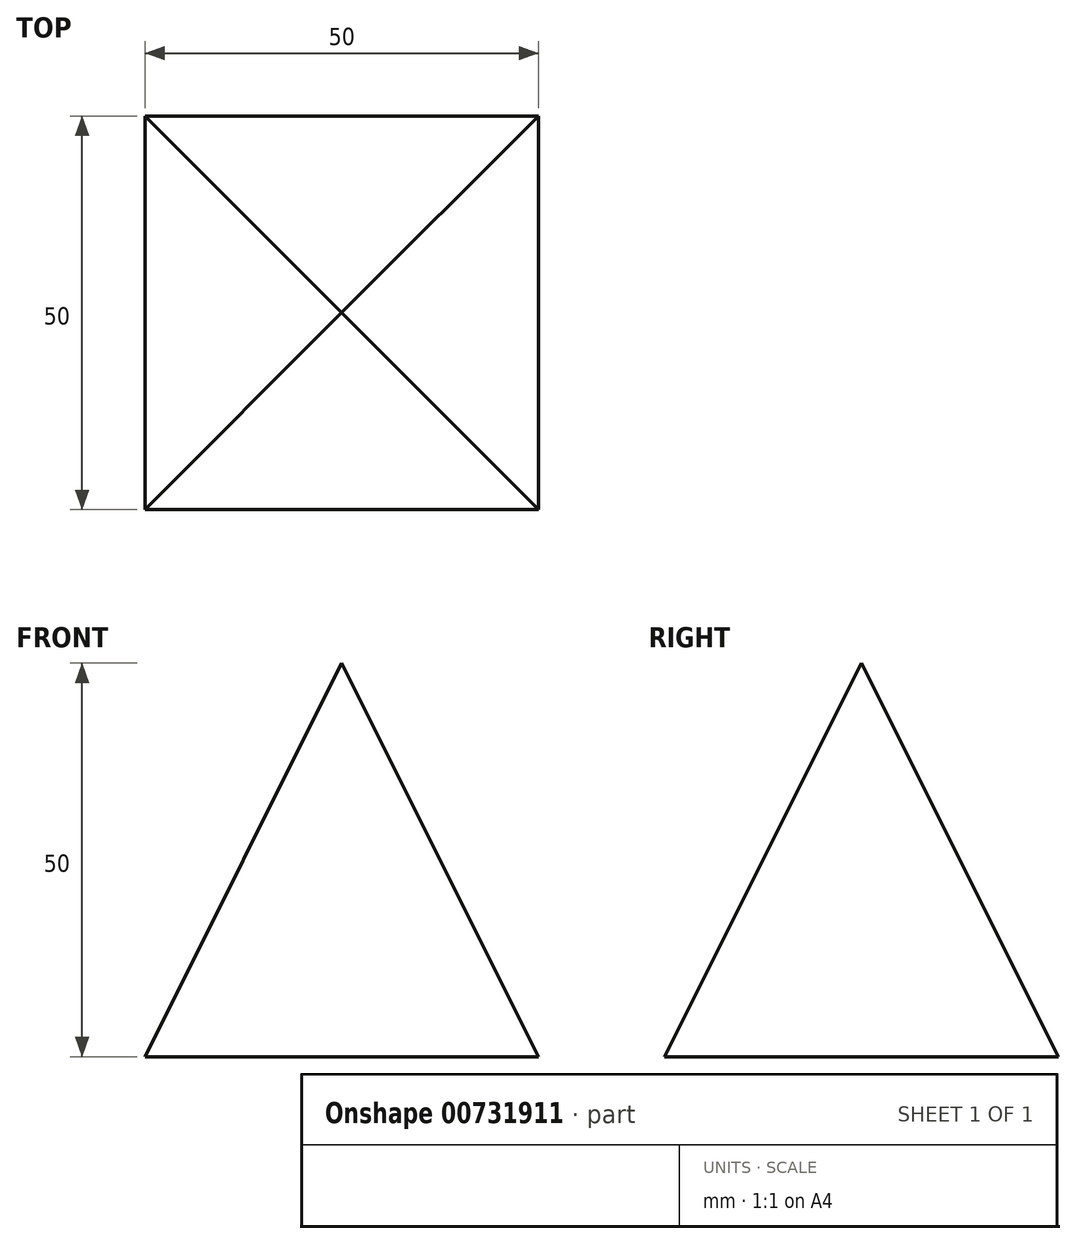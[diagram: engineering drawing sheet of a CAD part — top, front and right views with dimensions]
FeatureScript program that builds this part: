
annotation { "Feature Type Name" : "Feature", "Feature Type Description" : "" }
export const myFeature = defineFeature(function(context is Context, id is Id, definition is map)
    precondition{}
    {
        {
            var Q0;
            Q0=qCreatedBy(makeId("Top.planeOp"),FACE);
            var sketch = newSketch(context, id + "F0", { "sketchPlane" : qUnion([Q0])});
            skLineSegment(sketch, "E0.bottom", {"start": v(25, -25) * mm, "end": v(-25, -25) * mm});
            skLineSegment(sketch, "E0.top", {"start": v(25, 25) * mm, "end": v(-25, 25) * mm});
            skLineSegment(sketch, "E0.left", {"start": v(25, -25) * mm, "end": v(25, 25) * mm});
            skLineSegment(sketch, "E0.right", {"start": v(-25, -25) * mm, "end": v(-25, 25) * mm});
            skPoint(sketch, "E0.middle", {"position": v(0, 0) * mm});
            skSolve(sketch);
        }
        {
            var Q0;
            Q0=qCreatedBy(makeId("Top.planeOp"),FACE);
            cPlane(context, id + "F1", {"entities" : qUnion([Q0]), "cplaneType" : CPlaneType.OFFSET, "offset" : 50 * mm, "width" : 150 * mm, "height" : 150 * mm});
        }
        {
            var Q0;
            Q0=qCreatedBy(id+"F1.planeOp",FACE);
            var sketch = newSketch(context, id + "F2", { "sketchPlane" : qUnion([Q0])});
            skPoint(sketch, "E1.0", {"position": v(0, 0) * mm});
            skSolve(sketch);
        }
        {
            var Q0;
            Q0=sQuery(id+"F2.wireOp",VERTEX,"E1.0");
            var Q1;
            Q1=makeQuery(id+"F0.imprint","IMPRINT",FACE,{"disambiguationData":[TD([[makeQuery(id+"F0.imprint","IMPRINT",EDGE,{"derivedFrom":sQuery(id+"F0.wireOp",EDGE,"E0.bottom")}),-1.0]])]});
            loft(context, id + "F3", {"sheetProfilesArray" : [{ "sheetProfileEntities" : qUnion([Q0]) }, { "sheetProfileEntities" : qUnion([Q1]) }]});
        }
    });
